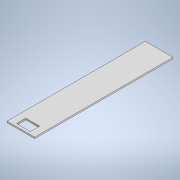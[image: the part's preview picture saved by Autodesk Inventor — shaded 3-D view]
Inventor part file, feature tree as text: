
AUTODESK INVENTOR PART (.ipt)
format: ipt  version: 2020.5 (Build 245400000, 400)  size: 107,008 bytes
history: native  units: mm
features: sketch x3, extrude x2, other x1
ambient origin geometry x8: Origin, YZ Plane, XZ Plane, XY Plane, X Axis, Y Axis, Z Axis, Center Point
bodies: Body1 (feature_tree)
feature tree (6):
  other  "Sólido1"
  sketch  "Boceto1"  dims[d0=152.4mm d1=762.0mm]
  extrude  "Extrusión1"  Depth=762.0mm
  extrude  "Extrusión2"  Depth=14.478mm
  sketch  "Boceto2"  dims[d2=7.62mm d3=0.0mm d4=14.478mm]
  sketch  "Boceto3"  dims[d5=76.2mm d6=50.8mm d7=0.0mm d8=25.4mm d9=0.0mm]
